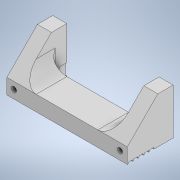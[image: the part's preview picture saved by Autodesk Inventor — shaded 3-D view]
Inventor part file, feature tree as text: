
AUTODESK INVENTOR PART (.ipt)
format: ipt  version: 2021 (Build 250183000, 183)  size: 710,656 bytes
history: native  units: in
note: dims shown in document units (in); Inventor stores cm internally (conversion verified against a paired STEP export)
features: sketch x8, extrude x7, projected_geometry x7, mirror x4, pattern_linear x3, fillet x2, chamfer x2, hole x1
ambient origin geometry x8: Origin, YZ Plane, XZ Plane, XY Plane, X Axis, Y Axis, Z Axis, Center Point
bodies: Solid1 (feature_tree)
feature tree (34):
  extrude  "Extrusion1"  Depth=0.5in
  extrude  "Extrusion2"  Depth=0.5in
  mirror  "Mirror1"
  fillet  "Fillet1"  Radius=0.5in
  extrude  "Extrusion3"  Depth=0.125in
  pattern_linear  "Rectangular Pattern1"  Count1=11 Spacing1=0.25in
  extrude  "Extrusion4"  Depth=0.375in
  mirror  "Mirror2"
  hole  "Hole1"  [1 undecoded]
  mirror  "Mirror3"
  extrude  "Extrusion5"  Depth=0.19in
  chamfer  "Chamfer2"  Distance=0.236in
  fillet  "Fillet3"  Radius=0.8108in
  chamfer  "Chamfer3"  Distance=1.0in
  extrude  "Extrusion9"  Depth=0.125in TaperAngle=45.0deg
  pattern_linear  "Rectangular Pattern5"  Spacing1=0.5in  [1 undecoded]
  extrude  "Extrusion10"  Depth=0.125in TaperAngle=45.0deg
  pattern_linear  "Rectangular Pattern6"  Spacing1=4.1in  [1 undecoded]
  mirror  "Mirror5"
  sketch  "Sketch1"  dims[d0=3.938in d1=0.5in]
  sketch  "Sketch2"  dims[d2=1.0in d3=0.0in d4=0.46in d5=0.5in d6=0.0in]
  projected_geometry  "Projected Loop1"
  sketch  "Sketch3"  dims[d7=0.125in d9=0.162in]
  projected_geometry  "Projected Loop2"
  sketch  "Sketch4"  dims[d10=0.087in]
  projected_geometry  "Projected Loop3"
  projected_geometry  "Projected Loop4"
  sketch  "Sketch5"  dims[d11=0.0625in d12=0.0in d13=4.3307in d15=0.25in]
  projected_geometry  "Projected Loop5"
  projected_geometry  "Projected Loop6"
  sketch  "Sketch6"  dims[d19=0.04in d20=0.375in]
  projected_geometry  "Projected Loop7"
  sketch  "Sketch9"  dims[d21=0.02in d22=0.25in d23=0.0in]
  sketch  "Sketch10"  dims[d24=0.266in d25=0.276in d26=0.236in d27=0.17in d28=0.75in d29=0.507in d30=0.25in d31=0.5635in d32=0.12in d33=0.8108in d34=1.0in d35=0.0in d36=1.0in d37=0.125in d38=45.0deg d39=0.5in d41=0.01in d42=0.125in d43=45.0deg d71=4.1in d72=0.15in d73=0.125in d74=2.05in d75=0.05in d76=-0.1031in d77=1.9685in d79=0.175in d80=0.125in d81=0.51in d82=0.05in d83=0.05in d84=0.0in d85=0.7874in d87=0.19in]
note: 3 required parameter values undecoded (feature->parameter linkage not recoverable at this tier; creation-order binding heuristic only, values carry confidence <= 0.55)
